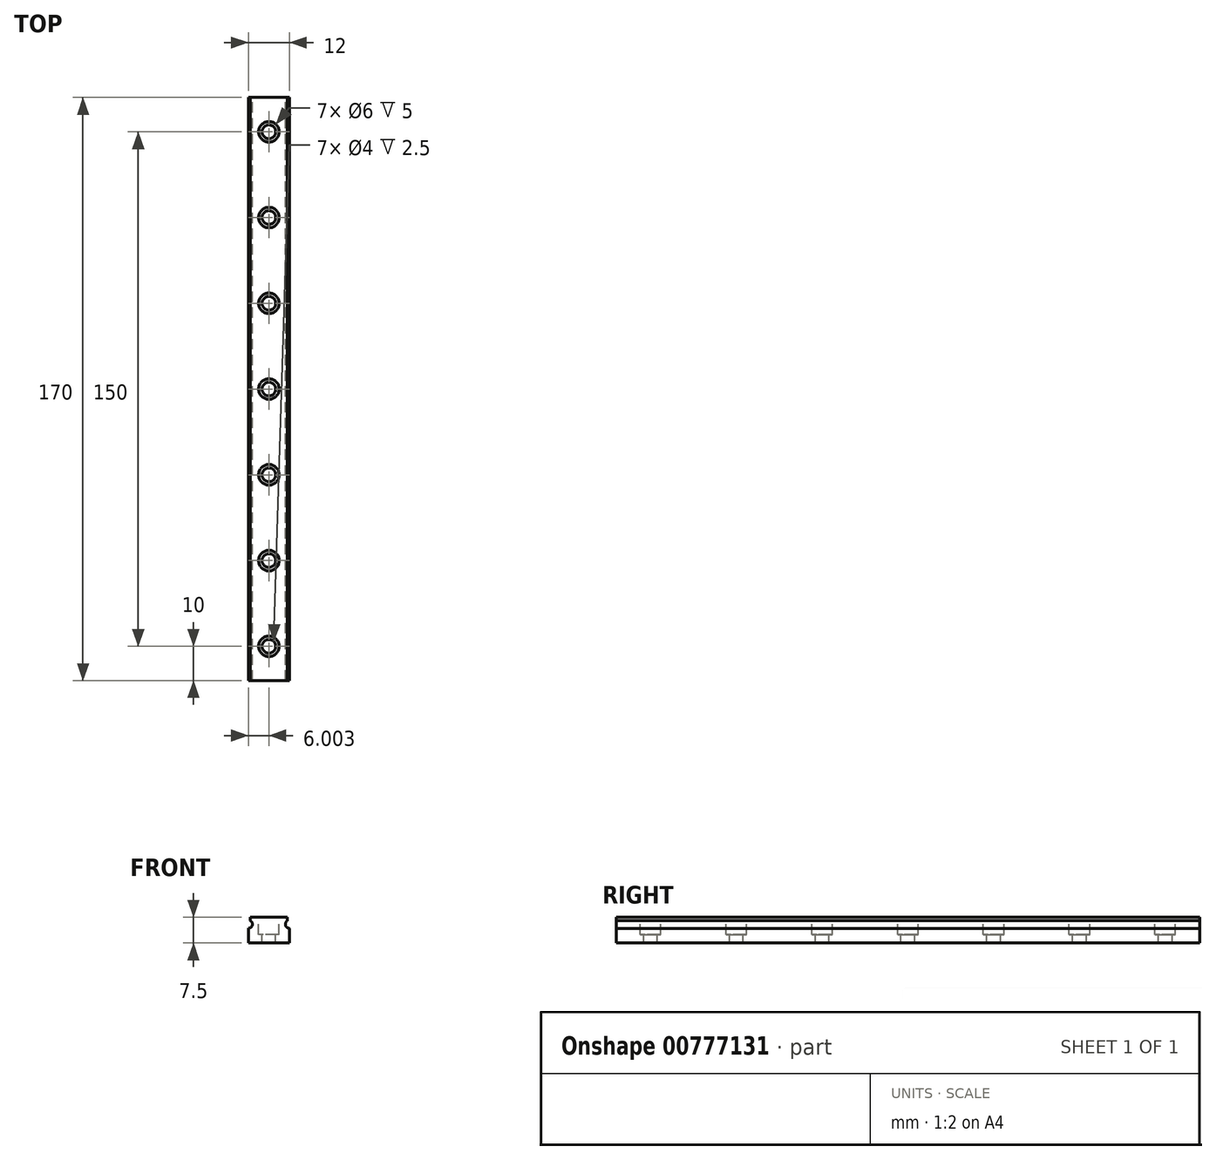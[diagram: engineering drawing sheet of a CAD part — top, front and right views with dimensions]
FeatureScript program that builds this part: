
annotation { "Feature Type Name" : "Feature", "Feature Type Description" : "" }
export const myFeature = defineFeature(function(context is Context, id is Id, definition is map)
    precondition{}
    {
        {
            var Q0;
            Q0=qCreatedBy(makeId("Front.planeOp"),FACE);
            var sketch = newSketch(context, id + "F0", { "sketchPlane" : qUnion([Q0])});
            skLineSegment(sketch, "E0.bottom", {"start": v(-56.4, 32.45) * mm, "end": v(-44.4, 32.45) * mm});
            skLineSegment(sketch, "E0.top", {"start": v(-56.4, 24.95) * mm, "end": v(-44.4, 24.95) * mm});
            skLineSegment(sketch, "E0.left", {"start": v(-56.4, 32.45) * mm, "end": v(-56.4, 24.95) * mm});
            skLineSegment(sketch, "E0.right", {"start": v(-44.4, 32.45) * mm, "end": v(-44.4, 24.95) * mm});
            skLineSegment(sketch, "E1", {"start": v(-45, 32.45) * mm, "end": v(-45, 31.45) * mm});
            skLineSegment(sketch, "E2", {"start": v(-45, 31.45) * mm, "end": v(-45.6, 30.43) * mm});
            skLineSegment(sketch, "E3", {"start": v(-45.6, 30.43) * mm, "end": v(-44.8, 29.96) * mm});
            skLineSegment(sketch, "E4", {"start": v(-44.8, 29.96) * mm, "end": v(-44.4, 29.25) * mm});
            skLineSegment(sketch, "E5", {"start": v(-55.8, 32.45) * mm, "end": v(-55.8, 31.45) * mm});
            skLineSegment(sketch, "E6", {"start": v(-55.8, 31.45) * mm, "end": v(-55.2, 31.08) * mm});
            skLineSegment(sketch, "E7", {"start": v(-55.2, 31.08) * mm, "end": v(-55.8, 30.1) * mm});
            skLineSegment(sketch, "E8", {"start": v(-55.8, 30.1) * mm, "end": v(-56.4, 29.25) * mm});
            skArc(sketch, "E9", {"start": v(-56.4, 29.25) * mm, "mid": v(-55.25, 30.11) * mm, "end": v(-55.8, 31.45) * mm});
            skArc(sketch, "E10", {"start": v(-45, 31.45) * mm, "mid": v(-45.57, 30.11) * mm, "end": v(-44.4, 29.25) * mm});
            skLineSegment(sketch, "E11", {"start": v(-55.8, 31.45) * mm, "end": v(-55.8, 32.45) * mm});
            skSolve(sketch);
        }
        {
            var Q0;
            {var subQ13=sQuery(id+"F0.wireOp",EDGE,"E0.top");Q0=makeQuery(id+"F0.imprint","IMPRINT",FACE,{"disambiguationData":[TD([[makeQuery(id+"F0.imprint","IMPRINT",EDGE,{"derivedFrom":subQ13}),1.0]])]});}
            var Q1;
            {var subQ0=sQuery(id+"F0.wireOp",EDGE,"E6");Q1=makeQuery(id+"F0.imprint","IMPRINT",FACE,{"disambiguationData":[TD([[makeQuery(id+"F0.imprint","IMPRINT",EDGE,{"derivedFrom":subQ0}),-1.0]])]});}
            extrude(context, id + "F1", {"entities" : qUnion([Q0, Q1]), "depth" : 170 * mm, "offsetDistance" : 25 * mm});
        }
        {
            var Q0;
            Q0=makeQuery(id+"F1.opExtrude","SWEPT_FACE",FACE,{"disambiguationData":[OSD([sQuery(id+"F0.wireOp",EDGE,"E0.bottom")])]});
            var sketch = newSketch(context, id + "F2", { "sketchPlane" : qUnion([Q0])});
            skCircle(sketch, "E12", {"center": v(-50.4, -160) * mm, "radius": 3 * mm});
            skPoint(sketch, "E12.centerSnap0", {"position": v(-50.4, -170) * mm});
            skCircle(sketch, "E13", {"center": v(-50.4, -135) * mm, "radius": 3 * mm});
            skCircle(sketch, "E14", {"center": v(-50.4, -110) * mm, "radius": 3 * mm});
            skCircle(sketch, "E15", {"center": v(-50.4, -85) * mm, "radius": 3 * mm});
            skCircle(sketch, "E16", {"center": v(-50.4, -60) * mm, "radius": 3 * mm});
            skCircle(sketch, "E17", {"center": v(-50.4, -35) * mm, "radius": 3 * mm});
            skCircle(sketch, "E18", {"center": v(-50.4, -10) * mm, "radius": 3 * mm});
            skCircle(sketch, "E19", {"center": v(-50.4, -160) * mm, "radius": 2 * mm});
            skCircle(sketch, "E20", {"center": v(-50.4, -135) * mm, "radius": 2 * mm});
            skCircle(sketch, "E21", {"center": v(-50.4, -110) * mm, "radius": 2 * mm});
            skCircle(sketch, "E22", {"center": v(-50.4, -85) * mm, "radius": 2 * mm});
            skCircle(sketch, "E23", {"center": v(-50.4, -60) * mm, "radius": 2 * mm});
            skCircle(sketch, "E24", {"center": v(-50.4, -35) * mm, "radius": 2 * mm});
            skCircle(sketch, "E25", {"center": v(-50.4, -10) * mm, "radius": 2 * mm});
            skSolve(sketch);
        }
        {
            var Q0;
            Q0 = qSketchRegion(id + "F2", true);
            extrude(context, id + "F3", {"entities" : qUnion([Q0]), "operationType" : NewBodyOperationType.REMOVE, "oppositeDirection" : true, "depth" : 5 * mm, "offsetDistance" : 25 * mm});
        }
        {
            var Q0;
            Q0=makeQuery(id+"F2.imprint","IMPRINT",FACE,{"disambiguationData":[TD([[makeQuery(id+"F2.imprint","IMPRINT",EDGE,{"derivedFrom":sQuery(id+"F2.wireOp",EDGE,"E19")}),1.0]])]});
            var Q1;
            Q1=makeQuery(id+"F2.imprint","IMPRINT",FACE,{"disambiguationData":[TD([[makeQuery(id+"F2.imprint","IMPRINT",EDGE,{"derivedFrom":sQuery(id+"F2.wireOp",EDGE,"E20")}),1.0]])]});
            var Q2;
            Q2=makeQuery(id+"F2.imprint","IMPRINT",FACE,{"disambiguationData":[TD([[makeQuery(id+"F2.imprint","IMPRINT",EDGE,{"derivedFrom":sQuery(id+"F2.wireOp",EDGE,"E21")}),1.0]])]});
            var Q3;
            Q3=makeQuery(id+"F2.imprint","IMPRINT",FACE,{"disambiguationData":[TD([[makeQuery(id+"F2.imprint","IMPRINT",EDGE,{"derivedFrom":sQuery(id+"F2.wireOp",EDGE,"E22")}),1.0]])]});
            var Q4;
            Q4=makeQuery(id+"F2.imprint","IMPRINT",FACE,{"disambiguationData":[TD([[makeQuery(id+"F2.imprint","IMPRINT",EDGE,{"derivedFrom":sQuery(id+"F2.wireOp",EDGE,"E23")}),1.0]])]});
            var Q5;
            Q5=makeQuery(id+"F2.imprint","IMPRINT",FACE,{"disambiguationData":[TD([[makeQuery(id+"F2.imprint","IMPRINT",EDGE,{"derivedFrom":sQuery(id+"F2.wireOp",EDGE,"E24")}),1.0]])]});
            var Q6;
            Q6=makeQuery(id+"F2.imprint","IMPRINT",FACE,{"disambiguationData":[TD([[makeQuery(id+"F2.imprint","IMPRINT",EDGE,{"derivedFrom":sQuery(id+"F2.wireOp",EDGE,"E25")}),1.0]])]});
            extrude(context, id + "F4", {"entities" : qUnion([Q0, Q1, Q2, Q3, Q4, Q5, Q6]), "operationType" : NewBodyOperationType.REMOVE, "endBound" : BoundingType.THROUGH_ALL, "oppositeDirection" : true, "depth" : 25 * mm, "offsetDistance" : 25 * mm});
        }
    });
